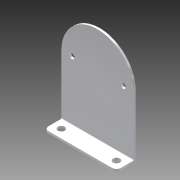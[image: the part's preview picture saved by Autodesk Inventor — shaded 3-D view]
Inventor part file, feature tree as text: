
AUTODESK INVENTOR PART (.ipt)
format: ipt  version: 2014 (Build 180170000, 170)  size: 115,200 bytes
history: native  units: in
note: dims shown in document units (in); Inventor stores cm internally (conversion verified against a paired STEP export)
features: fillet x3, hole x3, sketch x3, extrude x2, reference x2
ambient origin geometry x8: Origin, YZ Plane, XZ Plane, XY Plane, X Axis, Y Axis, Z Axis, Center Point
bodies: Solid1 (feature_tree)
feature tree (13):
  extrude  "Extrusion1"  Depth=0.0625in
  extrude  "Extrusion2"  Depth=0.125in
  fillet  "Fillet1"  Radius=0.0312in
  hole  "Hole1"  [1 undecoded]
  fillet  "Fillet2"  Radius=0.75in
  hole  "Hole2"  [1 undecoded]
  hole  "Hole3"  [1 undecoded]
  fillet  "Fillet3"  [1 undecoded]
  sketch  "Sketch1"  dims[d0=0.0625in d1=0.0in d2=0.0625in]
  reference  "Reference1"
  sketch  "Sketch2"  dims[d3=0.5in d4=0.0in d5=0.125in]
  sketch  "Sketch3"  dims[d6=0.25in d16=0.25in d8=0.201in d9=0.75in d10=0.385in d11=0.25in d12=0.5635in d13=1.0in d14=0.8108in d15=0.0312in d17=0.25in d18=0.25in d19=0.201in d20=0.75in d21=0.385in d22=0.25in d23=0.5635in d24=1.0in d25=0.8108in d26=0.75in d27=0.75in d28=0.15in d29=0.75in d30=0.385in d31=0.25in d32=0.5635in d33=1.0in d34=0.8108in d35=0.125in]
  reference  "Reference3"
note: 4 required parameter values undecoded (feature->parameter linkage not recoverable at this tier; creation-order binding heuristic only, values carry confidence <= 0.55)
